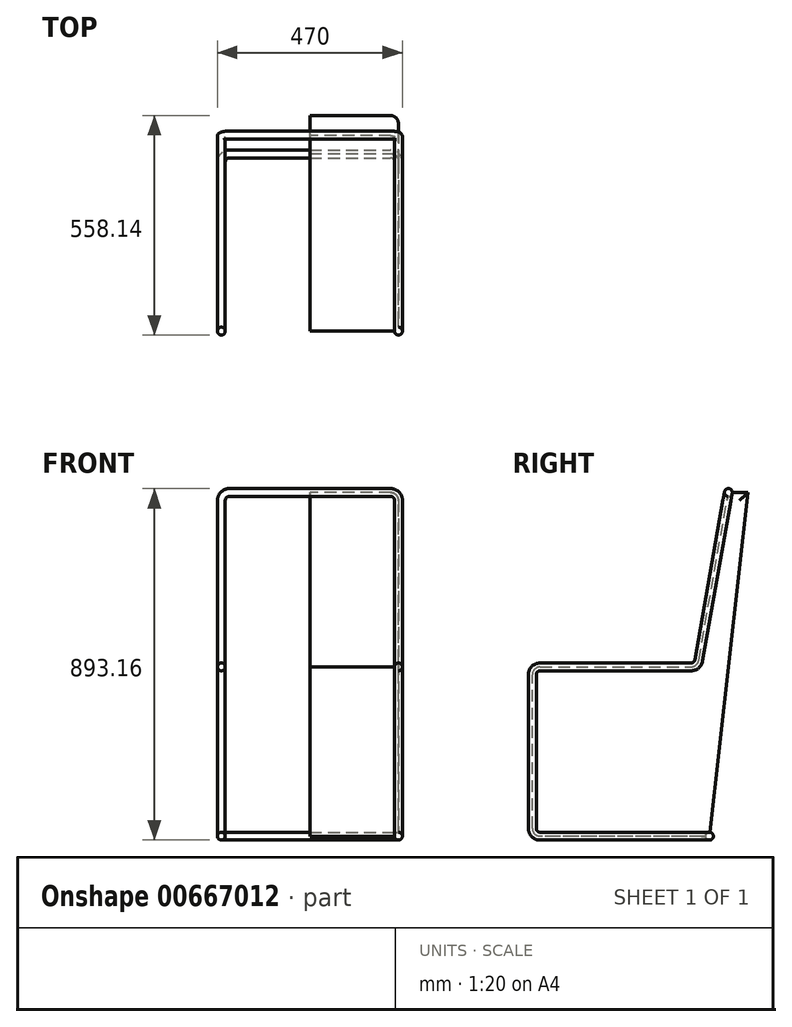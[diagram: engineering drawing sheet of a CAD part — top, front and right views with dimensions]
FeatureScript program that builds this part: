
annotation { "Feature Type Name" : "Feature", "Feature Type Description" : "" }
export const myFeature = defineFeature(function(context is Context, id is Id, definition is map)
    precondition{}
    {
        {
            var Q0;
            Q0=qCreatedBy(makeId("Right.planeOp"),FACE);
            var sketch = newSketch(context, id + "F0", { "sketchPlane" : qUnion([Q0])});
            skLineSegment(sketch, "E0", {"start": v(0, 0) * mm, "end": v(-450, 0) * mm});
            skLineSegment(sketch, "E1", {"start": v(-450, 0) * mm, "end": v(-450, 430) * mm});
            skLineSegment(sketch, "E2", {"start": v(-450, 430) * mm, "end": v(-30, 430) * mm});
            skLineSegment(sketch, "E3", {"start": v(-30, 430) * mm, "end": v(48.14, 873.16) * mm});
            skLineSegment(sketch, "E4", {"start": v(48.14, 873.16) * mm, "end": v(98.14, 873.16) * mm});
            skLineSegment(sketch, "E5", {"start": v(98.14, 873.16) * mm, "end": v(0, 0) * mm});
            skSolve(sketch);
        }
        {
            var Q0;
            Q0 = qSketchRegion(id + "F0", true);
            extrude(context, id + "F1", {"entities" : qUnion([Q0]), "depth" : 225 * mm, "offsetDistance" : 25.4 * mm});
        }
        {
            var Q0;
            Q0=makeQuery(id+"F1.opExtrude","CAP_EDGE",EDGE,{"disambiguationData":[OSD([sQuery(id+"F0.wireOp",EDGE,"E4")])],"isStart":false});
            var Q1;
            Q1=makeQuery(id+"F1.opExtrude","CAP_EDGE",EDGE,{"disambiguationData":[OSD([sQuery(id+"F0.wireOp",EDGE,"E5")])],"isStart":false});
            var Q2;
            Q2=makeQuery(id+"F1.opExtrude","SWEPT_EDGE",EDGE,{"disambiguationData":[OSD([sQuery(id+"F0.wireOp",EDGE,"E2"),sQuery(id+"F0.wireOp",EDGE,"E3")])]});
            var Q3;
            Q3=makeQuery(id+"F1.opExtrude","SWEPT_EDGE",EDGE,{"disambiguationData":[OSD([sQuery(id+"F0.wireOp",EDGE,"E1"),sQuery(id+"F0.wireOp",EDGE,"E2")])]});
            var Q4;
            Q4=makeQuery(id+"F1.opExtrude","SWEPT_EDGE",EDGE,{"disambiguationData":[OSD([sQuery(id+"F0.wireOp",EDGE,"E0"),sQuery(id+"F0.wireOp",EDGE,"E1")])]});
            fillet(context, id + "F2", {"entities" : qUnion([Q0, Q1, Q2, Q3, Q4]), "radius" : 20 * mm, "tangentPropagation" : true, "allowEdgeOverflow" : false});
        }
        {
            var Q0;
            Q0=makeQuery(id+"F1.opExtrude","CAP_FACE",FACE,{"disambiguationData":[OSD([sQuery(id+"F0.wireOp",EDGE,"E0"),sQuery(id+"F0.wireOp",EDGE,"E1"),sQuery(id+"F0.wireOp",EDGE,"E2"),sQuery(id+"F0.wireOp",EDGE,"E3"),sQuery(id+"F0.wireOp",EDGE,"E4"),sQuery(id+"F0.wireOp",EDGE,"E5")])],"isStart":false});
            var sketch = newSketch(context, id + "F3", { "sketchPlane" : qUnion([Q0])});
            skLineSegment(sketch, "E6.1", {"start": v(-27.09, 446.53) * mm, "end": v(44.62, 853.16) * mm});
            skLineSegment(sketch, "E6.2", {"start": v(-430, 430) * mm, "end": v(-46.78, 430) * mm});
            skLineSegment(sketch, "E6.3", {"start": v(-450, 20) * mm, "end": v(-450, 410) * mm});
            skLineSegment(sketch, "E6.4", {"start": v(-20.13, 0) * mm, "end": v(-430, 0) * mm});
            skArc(sketch, "E6.5", {"start": v(-27.09, 446.53) * mm, "mid": v(-33.93, 434.68) * mm, "end": v(-46.78, 430) * mm});
            skArc(sketch, "E6.6", {"start": v(-430, 430) * mm, "mid": v(-444.14, 424.14) * mm, "end": v(-450, 410) * mm});
            skArc(sketch, "E6.7", {"start": v(-450, 20) * mm, "mid": v(-444.14, 5.86) * mm, "end": v(-430, 0) * mm});
            skPoint(sketch, "E6.8", {"position": v(-450, 215) * mm});
            skSolve(sketch);
        }
        {
            var Q0;
            Q0=makeQuery(id+"F1.opExtrude","SWEPT_FACE",FACE,{"disambiguationData":[OSD([sQuery(id+"F0.wireOp",EDGE,"E3")])]});
            var sketch = newSketch(context, id + "F4", { "sketchPlane" : qUnion([Q0])});
            skLineSegment(sketch, "E7.1", {"start": v(205, 868.26) * mm, "end": v(0, 868.26) * mm});
            skEllipticalArc(sketch, "E7.2", {});
            const initialGuessF4  = {"E7.2": [0.205, 0.8479493562275268, 0, 1, 0.020308532237714897, 0.02, 4.71238898038469, 0]};
            skSetInitialGuess(sketch, initialGuessF4);
            skSolve(sketch);
        }
        {
            var Q0;
            Q0=makeQuery(id+"F1.opExtrude","SWEPT_FACE",FACE,{"disambiguationData":[OSD([sQuery(id+"F0.wireOp",EDGE,"E0")])]});
            var sketch = newSketch(context, id + "F5", { "sketchPlane" : qUnion([Q0])});
            skLineSegment(sketch, "E8.0", {"start": v(205, 0) * mm, "end": v(0, 0) * mm});
            skEllipticalArc(sketch, "E8.1", {});
            const initialGuessF5  = {"E8.1": [0.205, 0.020125936219912054, 0, 1, 0.02012593621991206, 0.02, 3.141592653589793, 4.71238898038469]};
            skSetInitialGuess(sketch, initialGuessF5);
            skSolve(sketch);
        }
        {
            var Q0;
            Q0=qCreatedBy(makeId("Right.planeOp"),FACE);
            var sketch = newSketch(context, id + "F6", { "sketchPlane" : qUnion([Q0])});
            skCircle(sketch, "E9", {"center": v(0, 0) * mm, "radius": 10 * mm});
            skSolve(sketch);
        }
        {
            var Q0;
            Q0=makeQuery(id+"F6.imprint","IMPRINT",FACE,{"disambiguationData":[TD([[makeQuery(id+"F6.imprint","IMPRINT",EDGE,{"derivedFrom":sQuery(id+"F6.wireOp",EDGE,"E9")}),1.0]])]});
            var Q1;
            Q1=sQuery(id+"F5.wireOp",EDGE,"E8.0");
            var Q2;
            Q2=sQuery(id+"F3.wireOp",EDGE,"E6.4");
            var Q3;
            Q3=sQuery(id+"F5.wireOp",EDGE,"E8.1");
            var Q4;
            Q4=sQuery(id+"F3.wireOp",EDGE,"E6.7");
            var Q5;
            Q5=sQuery(id+"F3.wireOp",EDGE,"E6.3");
            var Q6;
            Q6=sQuery(id+"F3.wireOp",EDGE,"E6.6");
            var Q7;
            Q7=sQuery(id+"F3.wireOp",EDGE,"E6.2");
            var Q8;
            Q8=sQuery(id+"F3.wireOp",EDGE,"E6.5");
            var Q9;
            Q9=sQuery(id+"F3.wireOp",EDGE,"E6.1");
            var Q10;
            Q10=sQuery(id+"F4.wireOp",EDGE,"E7.2");
            var Q11;
            Q11=sQuery(id+"F4.wireOp",EDGE,"E7.1");
            sweep(context, id + "F7", {"profiles" : qUnion([Q0]), "path" : qUnion([Q1, Q2, Q3, Q4, Q5, Q6, Q7, Q8, Q9, Q10, Q11])});
        }
        {
            var Q0;
            Q0=makeQuery(id+"F7.opSweep","SWEPT_BODY",BODY,{"disambiguationData":[OSD([sQuery(id+"F4.wireOp",EDGE,"E7.1"),sQuery(id+"F6.wireOp",EDGE,"E9")])]});
            var Q1;
            Q1=makeQuery(id+"F7.opSweep","CAP_FACE",FACE,{"disambiguationData":[OSD([sQuery(id+"F5.wireOp",VERTEX,"E8.0.end"),sQuery(id+"F6.wireOp",EDGE,"E9")])],"isStart":true});
            mirror(context, id + "F8", {"operationType" : NewBodyOperationType.ADD, "entities" : qUnion([Q0]), "mirrorPlane" : qUnion([Q1])});
        }
    });
